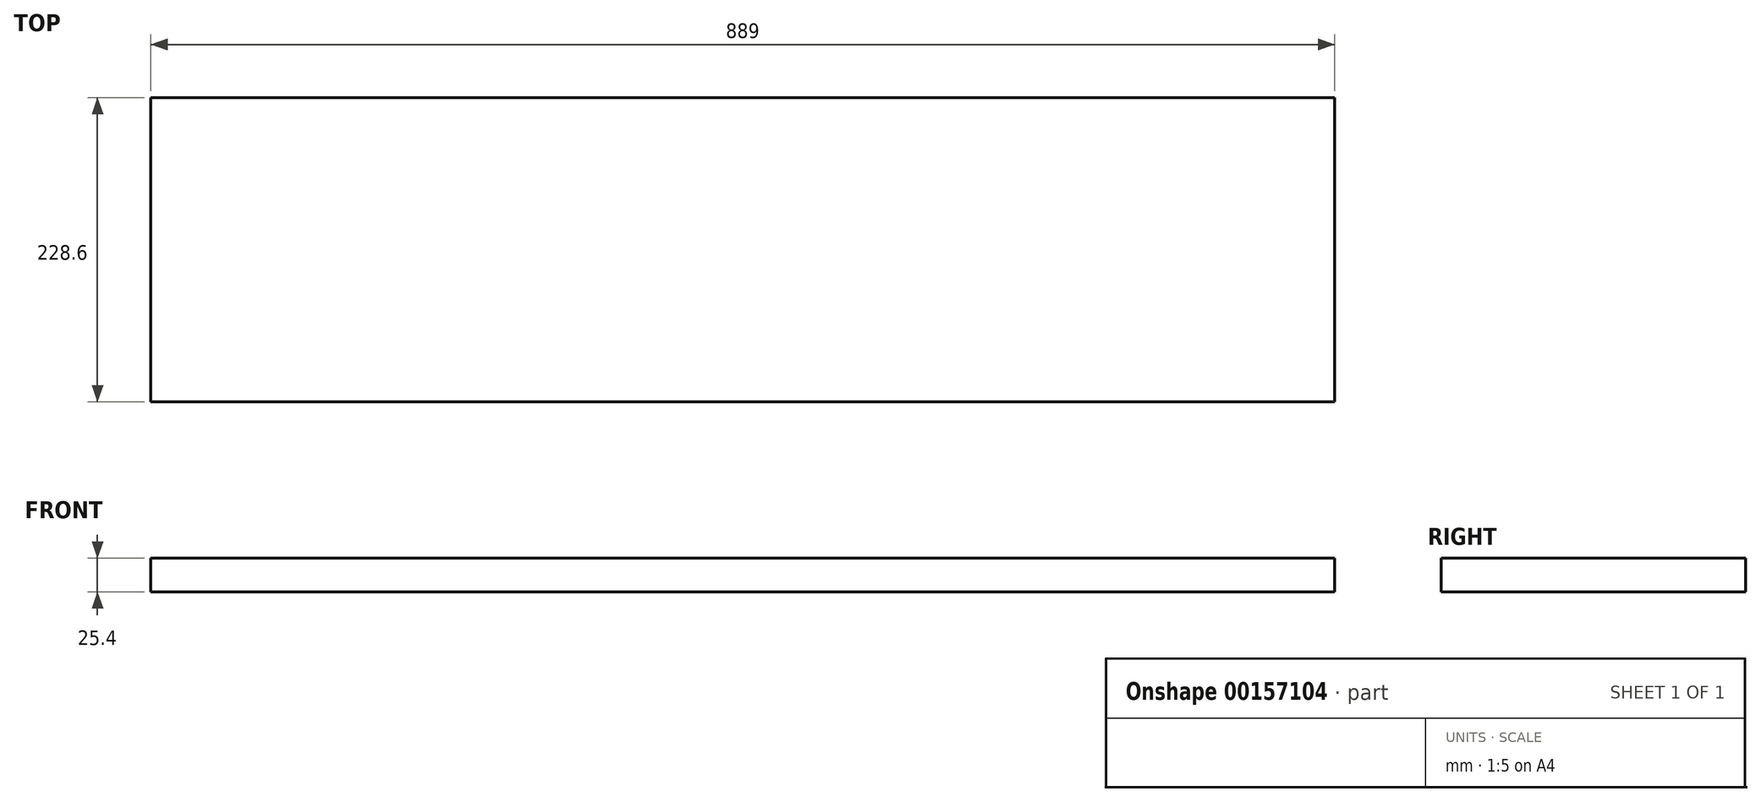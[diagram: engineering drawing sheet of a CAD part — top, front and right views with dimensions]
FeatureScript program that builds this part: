
annotation { "Feature Type Name" : "Feature", "Feature Type Description" : "" }
export const myFeature = defineFeature(function(context is Context, id is Id, definition is map)
    precondition{}
    {
        {
            var Q0;
            Q0=qCreatedBy(makeId("Top.planeOp"),FACE);
            var sketch = newSketch(context, id + "F0", { "sketchPlane" : qUnion([Q0])});
            skLineSegment(sketch, "E0.bottom", {"start": v(444.5, 114.3) * mm, "end": v(-444.5, 114.3) * mm});
            skLineSegment(sketch, "E0.top", {"start": v(444.5, -114.3) * mm, "end": v(-444.5, -114.3) * mm});
            skLineSegment(sketch, "E0.left", {"start": v(444.5, 114.3) * mm, "end": v(444.5, -114.3) * mm});
            skLineSegment(sketch, "E0.right", {"start": v(-444.5, 114.3) * mm, "end": v(-444.5, -114.3) * mm});
            skPoint(sketch, "E0.middle", {"position": v(0, 0) * mm});
            skSolve(sketch);
        }
        {
            var Q0;
            Q0 = qSketchRegion(id + "F0", true);
            extrude(context, id + "F1", {"entities" : qUnion([Q0]), "depth" : 25.4 * mm});
        }
    });
